# Revit family: 873-00-002-DN65-150
name_source: partatom
category: Pipe Accessories
units: mm (PartAtom-declared; Revit-internal decimal feet)

## family parameters
Always vertical = Yes
Cut with Voids When Loaded = No
Part Type = Valve - Breaks Into
Round Connector Dimension = Use Diameter
Shared = No
Work Plane-Based = No

## types (5) — shared parameters
873-0065-00-741000 = DN65_PN25
873-0080-00-741000 = DN80_PN25
873-0100-00-741000 = DN100_PN25
873-0125-00-741000 = DN125_PN25
873-0150-00-741000 = DN150_PN25
Body_Wallthicknss = 10 mm  [stored 0.0328084 ft]
Description_ = AVK DISMANTLING JOINT
Flange_thickness = 20 mm  [stored 0.0656168 ft]
Search_table = 873-00-002-DN65-150
URL product pages = https://www.avkvalves.com

## per-type parameters (varying)
| type | A | DN | Id(Radius) | L | T | d1 | d2 |
| DN065 | 190 mm  [stored 0.62336 ft] | 65 mm  [stored 0.213255 ft] | 33 mm | 330 mm  [stored 1.08268 ft] | 16 mm  [stored 0.0524934 ft] | 145 mm  [stored 0.475722 ft] | 93 mm |
| DN080 | 185 mm  [stored 0.606955 ft] | 80 mm  [stored 0.262467 ft] | 40 mm  [stored 0.131234 ft] | 340 mm  [stored 1.11549 ft] | 16 mm  [stored 0.0524934 ft] | 160 mm  [stored 0.524934 ft] | 100 mm  [stored 0.328084 ft] |
| DN100 | 195 mm  [stored 0.639764 ft] | 100 mm  [stored 0.328084 ft] | 50 mm  [stored 0.164042 ft] | 370 mm  [stored 1.21391 ft] | 20 mm  [stored 0.0656168 ft] | 190 mm  [stored 0.62336 ft] | 118 mm |
| DN125 | 195 mm  [stored 0.639764 ft] | 125 mm  [stored 0.410105 ft] | 63 mm | 380 mm  [stored 1.24672 ft] | 24 mm  [stored 0.0787402 ft] | 220 mm  [stored 0.721785 ft] | 135 mm  [stored 0.442913 ft] |
| DN150 | 205 mm  [stored 0.672572 ft] | 150 mm  [stored 0.492126 ft] | 75 mm | 380 mm  [stored 1.24672 ft] | 24 mm  [stored 0.0787402 ft] | 250 mm  [stored 0.82021 ft] | 150 mm  [stored 0.492126 ft] |

note: [stored X ft] marks values corroborated as IEEE doubles in the binary element streams (Revit-internal decimal feet)

## geometry (parser evidence)
native form markers: Sweep x5
no freeform markers — native parametric forms only
